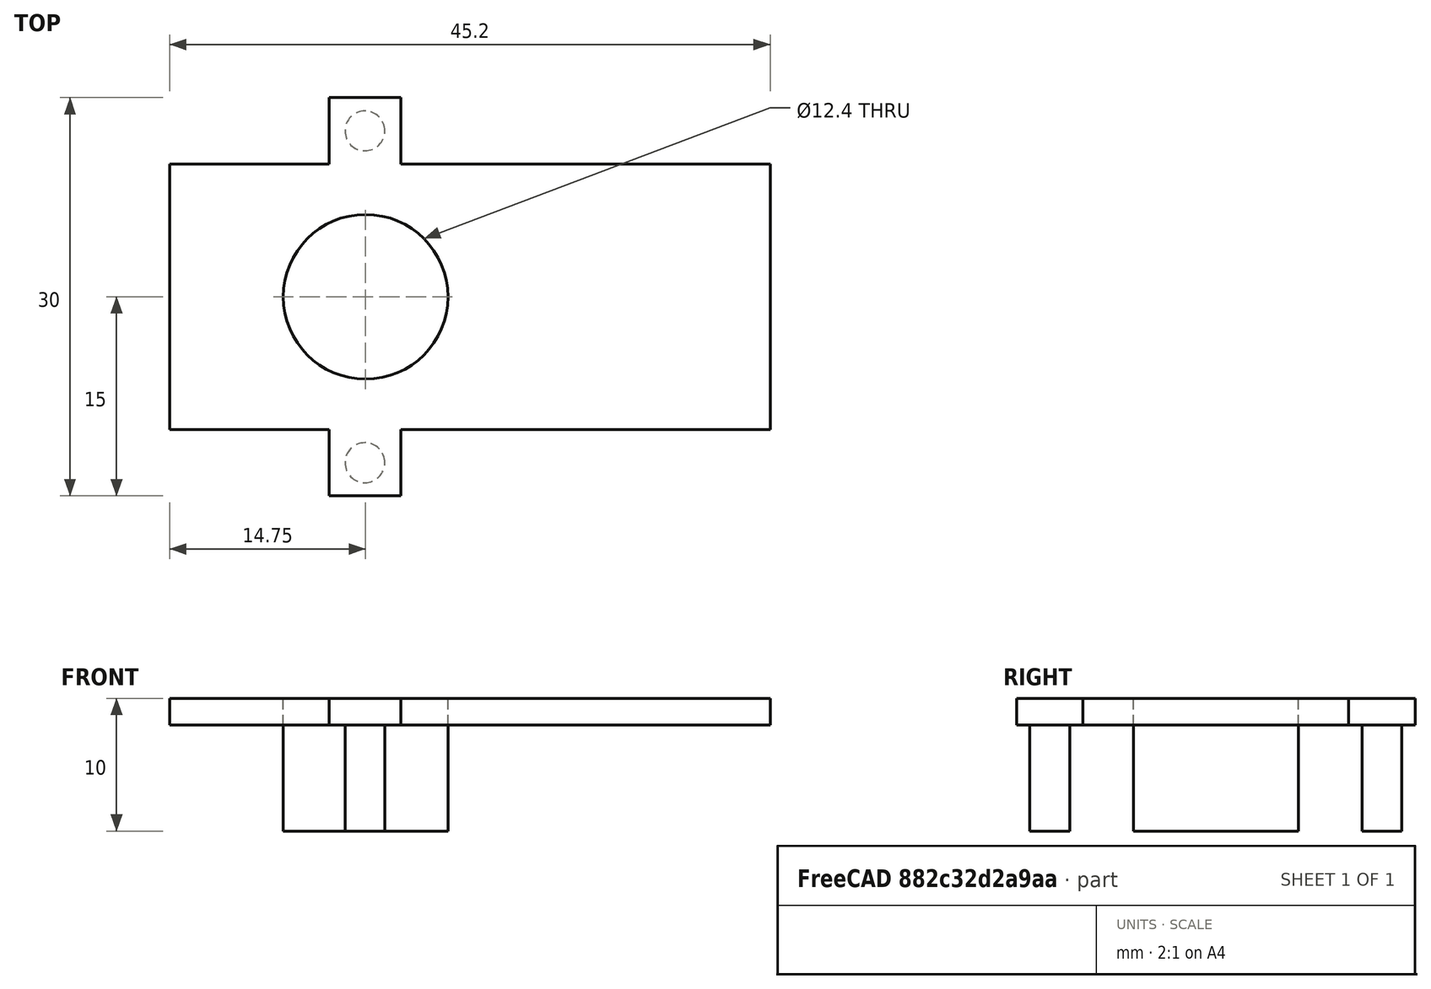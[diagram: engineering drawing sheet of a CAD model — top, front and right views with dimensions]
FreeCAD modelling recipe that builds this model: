
FCSTD DOCUMENT  (FreeCAD 0.17R13522 (Git))
Label: perforador_doble_encoder
License: All rights reserved
LicenseURL: http://en.wikipedia.org/wiki/All_rights_reserved
objects: Part::Fuse×4, Part::Cylinder×3, Part::Box×3, Part::FeaturePython×1
note: 11 computed .brp shape members not serialized (recipe doc carries the construction recipe); baked Part::Feature solids carry a one-line shape summary decoded from their .brp

FEATURE [Part::Cylinder] Cylinder  label="taladro1"
  Angle = 360
  AttacherType = Attacher::AttachEngine3D
  Height = 10
  Placement = pos=(-7.9,-12.5,-6) rot=(0,0,1;0rad)
  Radius = 1.5
FEATURE [Part::Cylinder] Cylinder001  label="taladro2"
  Angle = 360
  AttacherType = Attacher::AttachEngine3D
  Height = 10
  Placement = pos=(-7.9,12.5,-6) rot=(0,0,1;0rad)
  Radius = 1.5
FEATURE [Part::Box] Box  label="base"
  AttacherType = Attacher::AttachEngine3D
  Height = 2
  Length = 45.2
  Placement = pos=(-22.6,-10,2) rot=(0,0,1;0rad)
  Width = 20
FEATURE [Part::Box] Box001  label="oreja2"
  AttacherType = Attacher::AttachEngine3D
  Height = 2
  Length = 5.4
  Placement = pos=(-10.6,10,2) rot=(0,0,1;0rad)
  Width = 5
FEATURE [Part::Box] Box002  label="oreja1"
  AttacherType = Attacher::AttachEngine3D
  Height = 2
  Length = 5.4
  Placement = pos=(-10.6,-15,2) rot=(0,0,1;0rad)
  Width = 5
FEATURE [Part::Fuse] Fusion
  Base = -> Box
  Tool = -> Box002
FEATURE [Part::Fuse] Fusion001
  Base = -> Box001
  Tool = -> Fusion
FEATURE [Part::Fuse] Fusion002
  Base = -> Cylinder
  Tool = -> Fusion001
FEATURE [Part::Fuse] Fusion003  label="posicionador encoder doble"
  Base = -> Cylinder001
  Placement = pos=(0,0,-4) rot=(0,0,1;0rad)
  Tool = -> Fusion002
FEATURE [Part::Cylinder] Cylinder002  label="engranaje-bastago-grande"
  Angle = 360
  AttacherType = Attacher::AttachEngine3D
  Height = 10
  Placement = pos=(-7.85,0,-10) rot=(0,0,1;0rad)
  Radius = 6.2
FEATURE [Part::FeaturePython] BooleanFragments  label="posicion_encoder_doble"  # WARN: FeaturePython — macro-defined, semantics opaque (R4)
  Mode = 0
  Objects = -> [Fusion003,Cylinder002]
  Tolerance = 0
